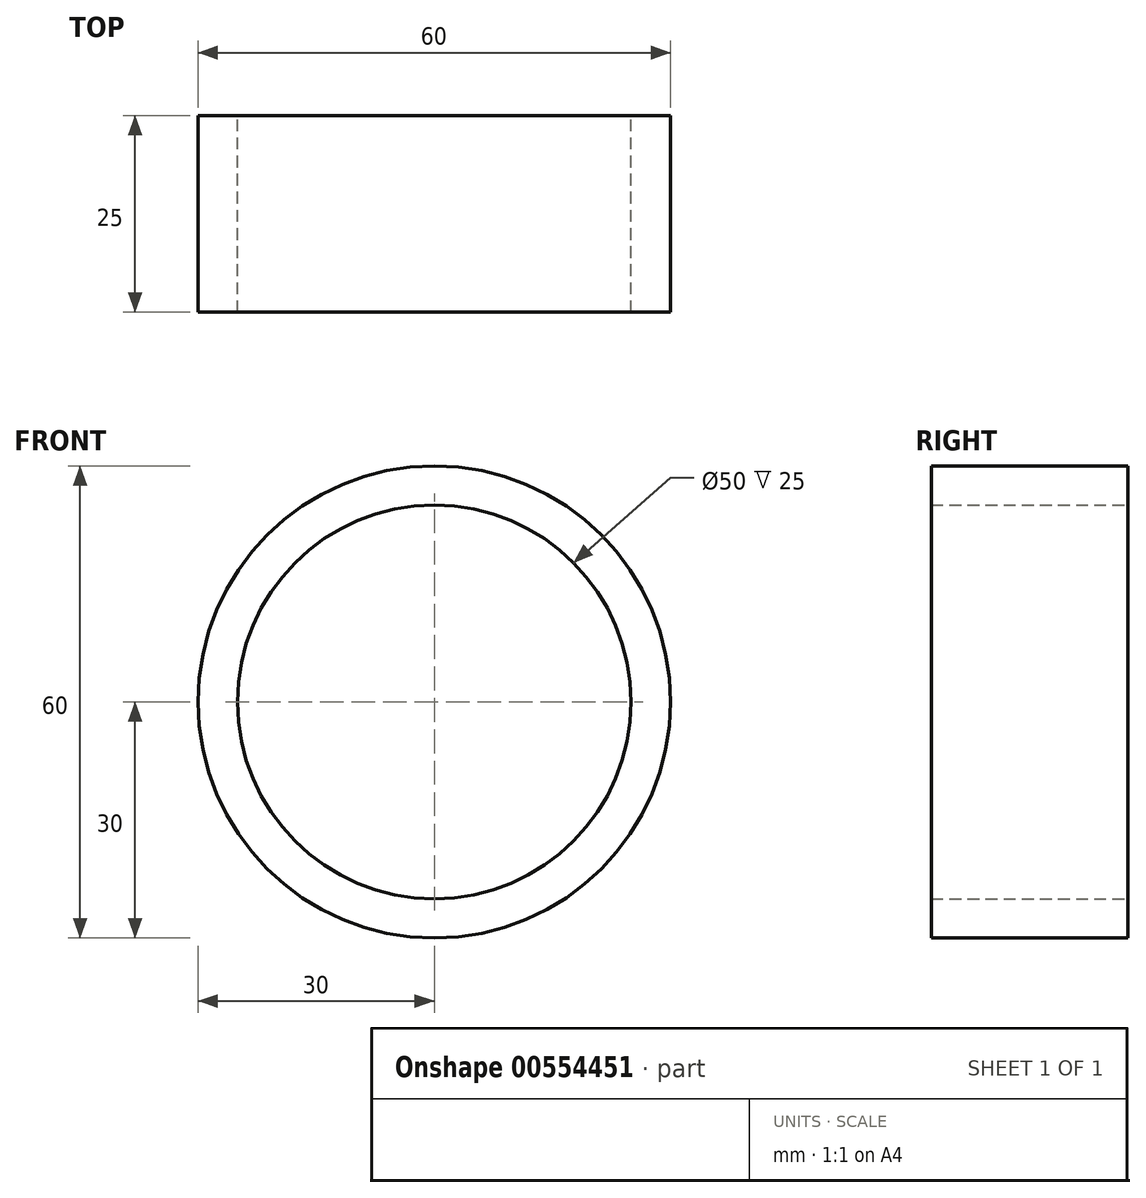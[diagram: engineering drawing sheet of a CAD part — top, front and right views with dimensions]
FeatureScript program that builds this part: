
annotation { "Feature Type Name" : "Feature", "Feature Type Description" : "" }
export const myFeature = defineFeature(function(context is Context, id is Id, definition is map)
    precondition{}
    {
        {
            var Q0;
            Q0=qCreatedBy(makeId("Front.planeOp"),FACE);
            var sketch = newSketch(context, id + "F0", { "sketchPlane" : qUnion([Q0])});
            skCircle(sketch, "E0", {"center": v(0, 0) * mm, "radius": 30 * mm});
            skCircle(sketch, "E1", {"center": v(0, 0) * mm, "radius": 25 * mm});
            skSolve(sketch);
        }
        {
            var Q0;
            Q0=makeQuery(id+"F0.imprint","IMPRINT",FACE,{"disambiguationData":[TD([[makeQuery(id+"F0.imprint","IMPRINT",EDGE,{"derivedFrom":sQuery(id+"F0.wireOp",EDGE,"E0")}),1.0]])]});
            extrude(context, id + "F1", {"entities" : qUnion([Q0]), "depth" : 25 * mm, "offsetDistance" : 25 * mm});
        }
    });
